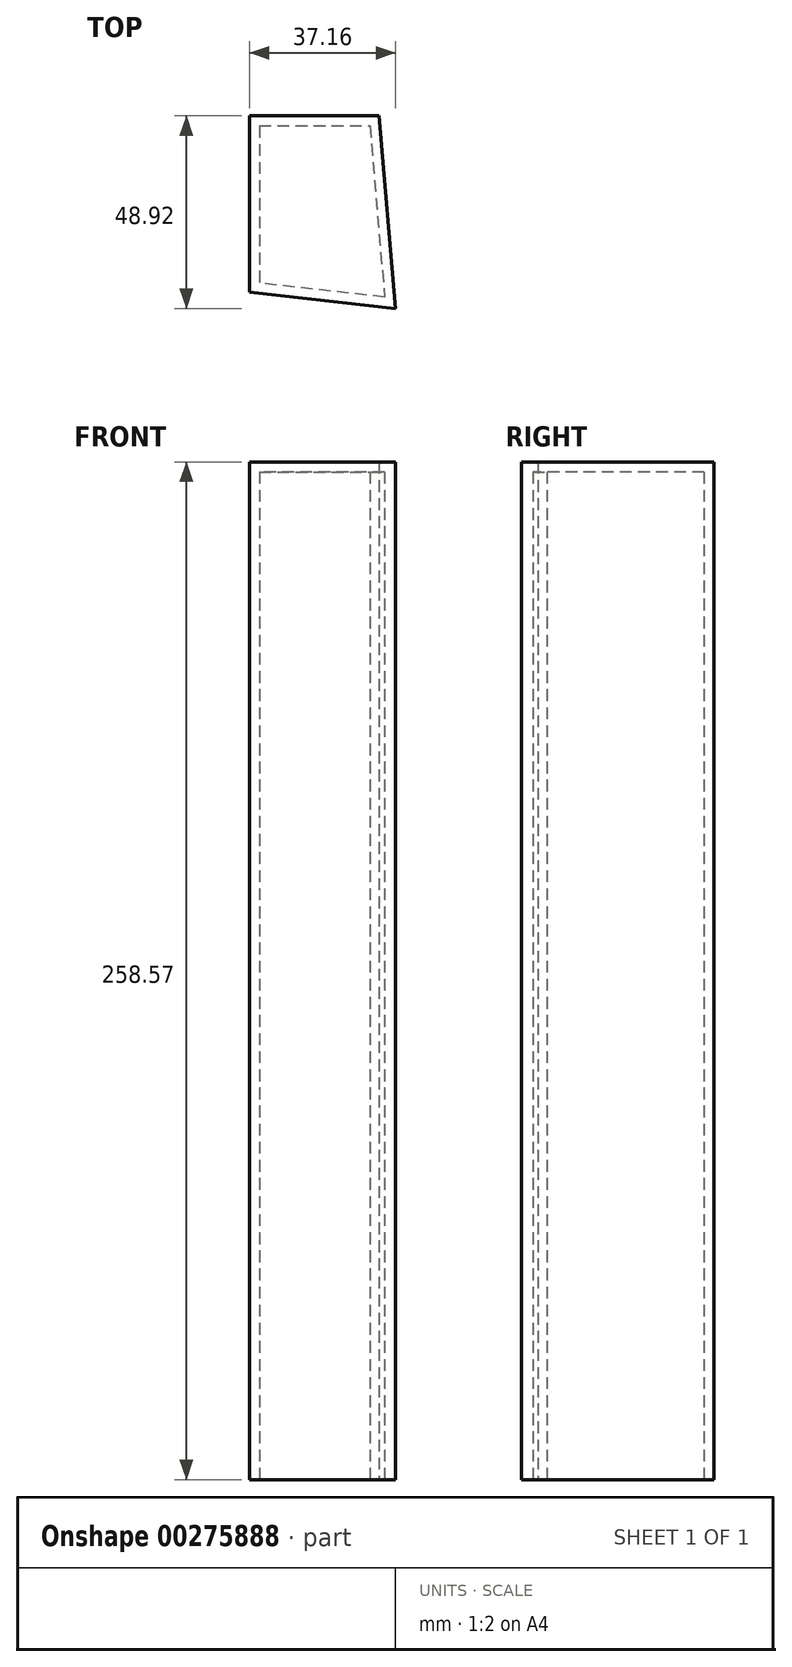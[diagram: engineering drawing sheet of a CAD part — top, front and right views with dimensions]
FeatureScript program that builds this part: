
annotation { "Feature Type Name" : "Feature", "Feature Type Description" : "" }
export const myFeature = defineFeature(function(context is Context, id is Id, definition is map)
    precondition{}
    {
        {
            var Q0;
            Q0=qCreatedBy(makeId("Top.planeOp"),FACE);
            var sketch = newSketch(context, id + "F0", { "sketchPlane" : qUnion([Q0])});
            skLineSegment(sketch, "E0", {"start": v(-129.18, 37.28) * mm, "end": v(-129.18, -7.51) * mm});
            skLineSegment(sketch, "E1", {"start": v(-129.18, 37.28) * mm, "end": v(-96.24, 37.28) * mm});
            skLineSegment(sketch, "E2", {"start": v(-96.24, 37.28) * mm, "end": v(-92.02, -11.64) * mm});
            skLineSegment(sketch, "E3", {"start": v(-92.02, -11.64) * mm, "end": v(-129.18, -7.51) * mm});
            skSolve(sketch);
        }
        {
            var Q0;
            Q0 = qSketchRegion(id + "F0", true);
            extrude(context, id + "F1", {"entities" : qUnion([Q0]), "depth" : 25.4 * mm});
        }
        {
            var Q0;
            Q0 = qSketchRegion(id + "F0", true);
            extrude(context, id + "F2", {"entities" : qUnion([Q0]), "operationType" : NewBodyOperationType.ADD, "oppositeDirection" : true, "depth" : 233.17 * mm});
        }
        {
            var Q0;
            Q0=makeQuery(id+"F2.opExtrude","CAP_FACE",FACE,{"disambiguationData":[OSD([sQuery(id+"F0.wireOp",EDGE,"E0"),sQuery(id+"F0.wireOp",EDGE,"E1"),sQuery(id+"F0.wireOp",EDGE,"E2"),sQuery(id+"F0.wireOp",EDGE,"E3")])],"isStart":false});
            shell(context, id + "F3", {"entities" : qUnion([Q0]), "thickness" : 2.54 * mm});
        }
    });
